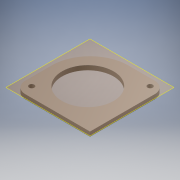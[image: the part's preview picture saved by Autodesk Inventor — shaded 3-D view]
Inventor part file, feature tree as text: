
AUTODESK INVENTOR PART (.ipt)
format: ipt  version: 2016 (Build 200138000, 138)  size: 412,672 bytes
history: native  units: mm
features: reference x2, plane x1, extrude x1, sketch x1
ambient origin geometry x8: Origin, YZ Plane, XZ Plane, XY Plane, X Axis, Y Axis, Z Axis, Center Point
bodies: Solid1 (feature_tree)
feature tree (5):
  plane  "Work Plane1"
  extrude  "Extrusion1"  [1 undecoded]
  sketch  "Sketch1"  dims[d0=3.0mm d1=0.0mm]
  reference  "Reference1"
  reference  "Reference2"
note: 1 required parameter value undecoded (feature->parameter linkage not recoverable at this tier; creation-order binding heuristic only, values carry confidence <= 0.55)
